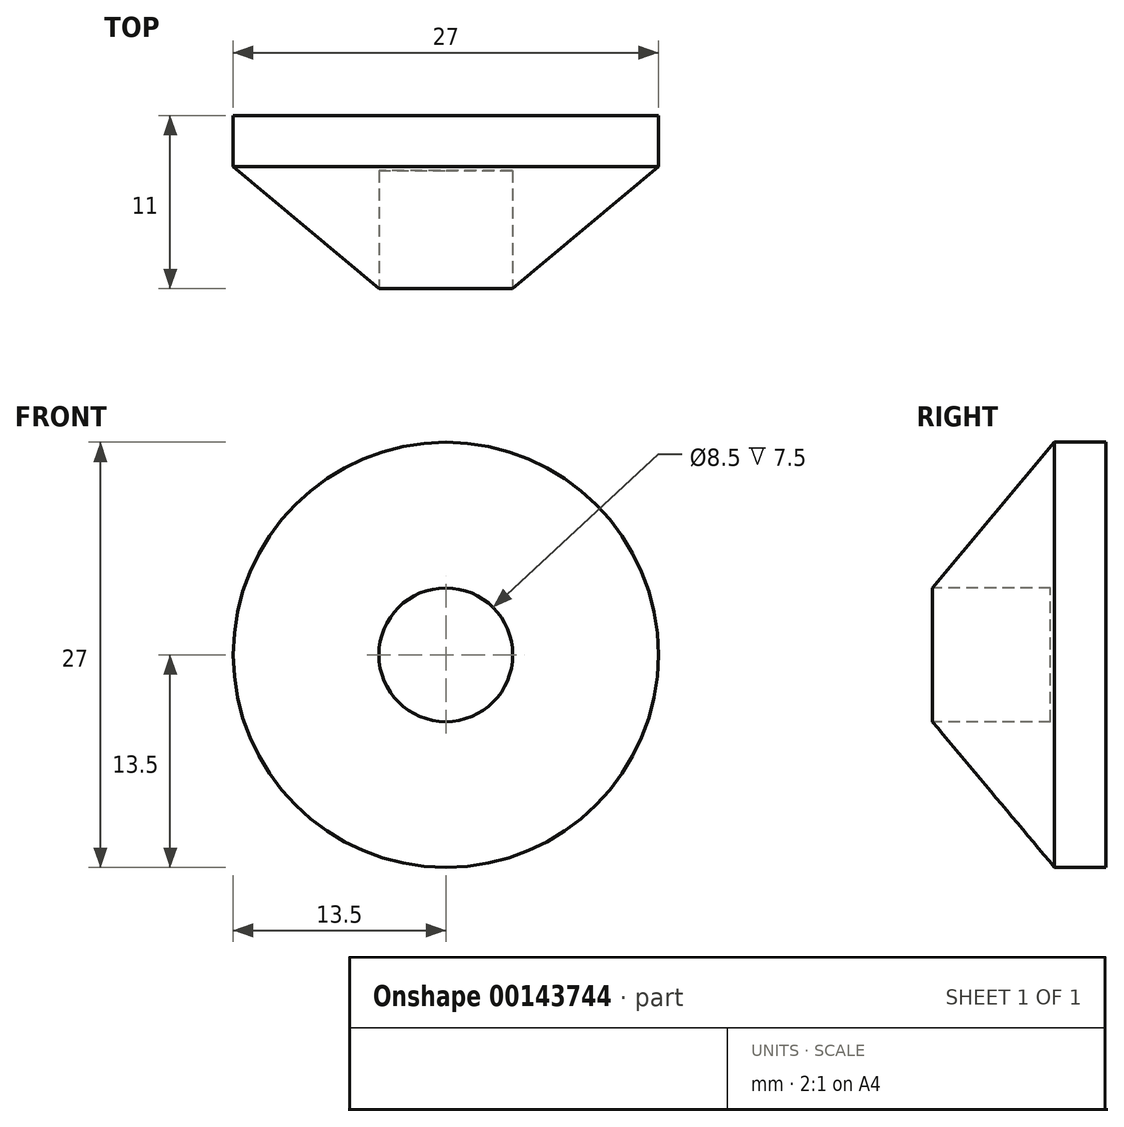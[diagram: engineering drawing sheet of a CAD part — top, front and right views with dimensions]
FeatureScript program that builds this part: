
annotation { "Feature Type Name" : "Feature", "Feature Type Description" : "" }
export const myFeature = defineFeature(function(context is Context, id is Id, definition is map)
    precondition{}
    {
        {
            var Q0;
            Q0=qCreatedBy(makeId("Front.planeOp"),FACE);
            var sketch = newSketch(context, id + "F0", { "sketchPlane" : qUnion([Q0])});
            skCircle(sketch, "E0", {"center": v(0, 0) * mm, "radius": 13.5 * mm});
            skSolve(sketch);
        }
        {
            var Q0;
            Q0=makeQuery(id+"F0.imprint","IMPRINT",FACE,{"disambiguationData":[TD([[makeQuery(id+"F0.imprint","IMPRINT",EDGE,{"derivedFrom":sQuery(id+"F0.wireOp",EDGE,"E0")}),1.0]])]});
            extrude(context, id + "F1", {"entities" : qUnion([Q0]), "depth" : 3.25 * mm});
        }
        {
            var Q0;
            Q0=qCreatedBy(makeId("Front.planeOp"),FACE);
            cPlane(context, id + "F2", {"entities" : qUnion([Q0]), "cplaneType" : CPlaneType.OFFSET, "offset" : 11 * mm, "width" : 152.4 * mm, "height" : 152.4 * mm});
        }
        {
            var Q0;
            Q0=qCreatedBy(id+"F2.planeOp",FACE);
            var sketch = newSketch(context, id + "F3", { "sketchPlane" : qUnion([Q0])});
            skCircle(sketch, "E1", {"center": v(0, 0) * mm, "radius": 4.25 * mm});
            skSolve(sketch);
        }
        {
            var Q0;
            Q0=makeQuery(id+"F3.imprint","IMPRINT",FACE,{"disambiguationData":[TD([[makeQuery(id+"F3.imprint","IMPRINT",EDGE,{"derivedFrom":sQuery(id+"F3.wireOp",EDGE,"E1")}),1.0]])]});
            var Q1;
            Q1=makeQuery(id+"F1.opExtrude","CAP_FACE",FACE,{"disambiguationData":[OSD([sQuery(id+"F0.wireOp",EDGE,"E0")])],"isStart":false});
            loft(context, id + "F4", {"operationType" : NewBodyOperationType.ADD, "sheetProfilesArray" : [{ "sheetProfileEntities" : qUnion([Q0]) }, { "sheetProfileEntities" : qUnion([Q1]) }]});
        }
        {
            var Q0;
            Q0=makeQuery(id+"F3.imprint","IMPRINT",FACE,{"disambiguationData":[TD([[makeQuery(id+"F3.imprint","IMPRINT",EDGE,{"derivedFrom":sQuery(id+"F3.wireOp",EDGE,"E1")}),1.0]])]});
            var sketch = newSketch(context, id + "F5", { "sketchPlane" : qUnion([Q0])});
            skCircle(sketch, "E2", {"center": v(0, 0) * mm, "radius": 4.25 * mm});
            skSolve(sketch);
        }
        {
            var Q0;
            Q0 = qSketchRegion(id + "F5", true);
            extrude(context, id + "F6", {"entities" : qUnion([Q0]), "operationType" : NewBodyOperationType.REMOVE, "oppositeDirection" : true, "depth" : 7.5 * mm});
        }
    });
